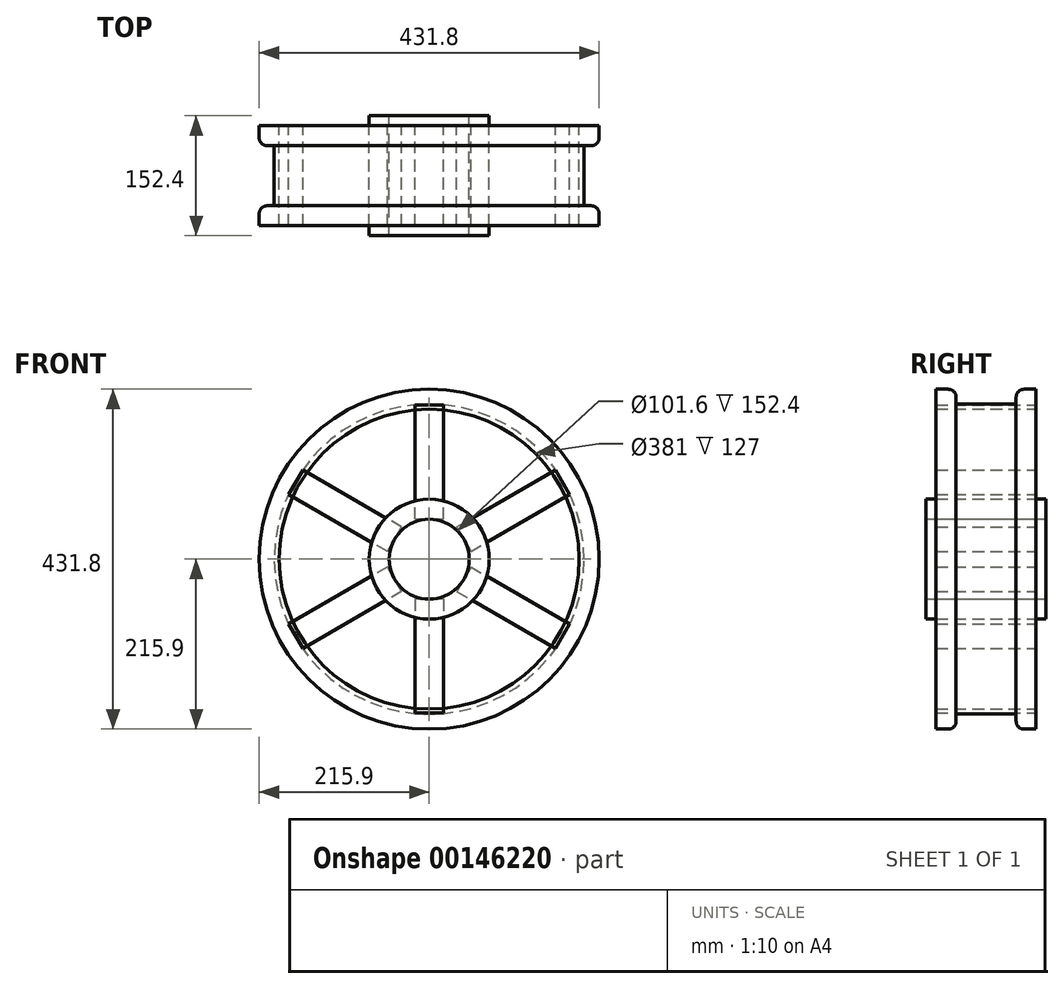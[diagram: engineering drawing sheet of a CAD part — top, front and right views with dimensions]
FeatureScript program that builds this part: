
annotation { "Feature Type Name" : "Feature", "Feature Type Description" : "" }
export const myFeature = defineFeature(function(context is Context, id is Id, definition is map)
    precondition{}
    {
        {
            var Q0;
            Q0=qCreatedBy(makeId("Front.planeOp"),FACE);
            var sketch = newSketch(context, id + "F0", { "sketchPlane" : qUnion([Q0])});
            skCircle(sketch, "E0", {"center": v(0, 0) * mm, "radius": 215.9 * mm});
            skCircle(sketch, "E1", {"center": v(0, 0) * mm, "radius": 190.5 * mm});
            skSolve(sketch);
        }
        {
            var Q0;
            Q0=makeQuery(id+"F0.imprint","IMPRINT",FACE,{"disambiguationData":[TD([[makeQuery(id+"F0.imprint","IMPRINT",EDGE,{"derivedFrom":sQuery(id+"F0.wireOp",EDGE,"E0")}),1.0]])]});
            extrude(context, id + "F1", {"entities" : qUnion([Q0]), "depth" : 127 * mm});
        }
        {
            var Q0;
            Q0=qCreatedBy(makeId("Front.planeOp"),FACE);
            var sketch = newSketch(context, id + "F2", { "sketchPlane" : qUnion([Q0])});
            skCircle(sketch, "E2", {"center": v(0, 0) * mm, "radius": 50.8 * mm});
            skCircle(sketch, "E3", {"center": v(0, 0) * mm, "radius": 76.2 * mm});
            skSolve(sketch);
        }
        {
            var Q0;
            Q0=makeQuery(id+"F2.imprint","IMPRINT",FACE,{"disambiguationData":[TD([[makeQuery(id+"F2.imprint","IMPRINT",EDGE,{"derivedFrom":sQuery(id+"F2.wireOp",EDGE,"E2")}),-1.0]])]});
            extrude(context, id + "F3", {"entities" : qUnion([Q0]), "depth" : 139.7 * mm});
        }
        {
            var Q0;
            Q0=makeQuery(id+"F3.opExtrude","CAP_FACE",FACE,{"disambiguationData":[OSD([sQuery(id+"F2.wireOp",EDGE,"E2"),sQuery(id+"F2.wireOp",EDGE,"E3")])],"isStart":true});
            extrude(context, id + "F4", {"entities" : qUnion([Q0]), "operationType" : NewBodyOperationType.ADD, "depth" : 12.7 * mm});
        }
        {
            var Q0;
            Q0=qCreatedBy(makeId("Front.planeOp"),FACE);
            var sketch = newSketch(context, id + "F5", { "sketchPlane" : qUnion([Q0])});
            skLineSegment(sketch, "E4", {"start": v(-17.98, 50.8) * mm, "end": v(17.98, 50.8) * mm});
            skLineSegment(sketch, "E5", {"start": v(17.98, 50.8) * mm, "end": v(17.98, 195.58) * mm});
            skLineSegment(sketch, "E6", {"start": v(17.98, 195.58) * mm, "end": v(-17.98, 195.58) * mm});
            skLineSegment(sketch, "E7", {"start": v(-17.98, 50.8) * mm, "end": v(-17.98, 195.58) * mm});
            skLineSegment(sketch, "E8.1.0", {"start": v(-160.39, 113.36) * mm, "end": v(-178.37, 82.22) * mm});
            skLineSegment(sketch, "E8.1.1", {"start": v(-35, 40.97) * mm, "end": v(-160.39, 113.36) * mm});
            skLineSegment(sketch, "E8.1.2", {"start": v(-52.99, 9.83) * mm, "end": v(-178.37, 82.22) * mm});
            skLineSegment(sketch, "E8.1.3", {"start": v(-52.99, 9.83) * mm, "end": v(-35, 40.97) * mm});
            skLineSegment(sketch, "E8.2.0", {"start": v(-178.37, -82.22) * mm, "end": v(-160.39, -113.36) * mm});
            skLineSegment(sketch, "E8.2.1", {"start": v(-52.99, -9.83) * mm, "end": v(-178.37, -82.22) * mm});
            skLineSegment(sketch, "E8.2.2", {"start": v(-35, -40.97) * mm, "end": v(-160.39, -113.36) * mm});
            skLineSegment(sketch, "E8.2.3", {"start": v(-35, -40.97) * mm, "end": v(-52.99, -9.83) * mm});
            skLineSegment(sketch, "E8.3.0", {"start": v(-17.98, -195.58) * mm, "end": v(17.98, -195.58) * mm});
            skLineSegment(sketch, "E8.3.1", {"start": v(-17.98, -50.8) * mm, "end": v(-17.98, -195.58) * mm});
            skLineSegment(sketch, "E8.3.2", {"start": v(17.98, -50.8) * mm, "end": v(17.98, -195.58) * mm});
            skLineSegment(sketch, "E8.3.3", {"start": v(17.98, -50.8) * mm, "end": v(-17.98, -50.8) * mm});
            skLineSegment(sketch, "E8.4.0", {"start": v(160.39, -113.36) * mm, "end": v(178.37, -82.22) * mm});
            skLineSegment(sketch, "E8.4.1", {"start": v(35, -40.97) * mm, "end": v(160.39, -113.36) * mm});
            skLineSegment(sketch, "E8.4.2", {"start": v(52.99, -9.83) * mm, "end": v(178.37, -82.22) * mm});
            skLineSegment(sketch, "E8.4.3", {"start": v(52.99, -9.83) * mm, "end": v(35, -40.97) * mm});
            skLineSegment(sketch, "E8.5.0", {"start": v(178.37, 82.22) * mm, "end": v(160.39, 113.36) * mm});
            skLineSegment(sketch, "E8.5.1", {"start": v(52.99, 9.83) * mm, "end": v(178.37, 82.22) * mm});
            skLineSegment(sketch, "E8.5.2", {"start": v(35, 40.97) * mm, "end": v(160.39, 113.36) * mm});
            skLineSegment(sketch, "E8.5.3", {"start": v(35, 40.97) * mm, "end": v(52.99, 9.83) * mm});
            skPoint(sketch, "E8.center", {"position": v(0, 0) * mm});
            skSolve(sketch);
        }
        {
            var Q0;
            Q0=makeQuery(id+"F5.imprint","IMPRINT",FACE,{"disambiguationData":[TD([[makeQuery(id+"F5.imprint","IMPRINT",EDGE,{"derivedFrom":sQuery(id+"F5.wireOp",EDGE,"E4")}),1.0]])]});
            var Q1;
            Q1=makeQuery(id+"F5.imprint","IMPRINT",FACE,{"disambiguationData":[TD([[makeQuery(id+"F5.imprint","IMPRINT",EDGE,{"derivedFrom":sQuery(id+"F5.wireOp",EDGE,"E8.1.0")}),1.0]])]});
            var Q2;
            Q2=makeQuery(id+"F5.imprint","IMPRINT",FACE,{"disambiguationData":[TD([[makeQuery(id+"F5.imprint","IMPRINT",EDGE,{"derivedFrom":sQuery(id+"F5.wireOp",EDGE,"E8.2.0")}),1.0]])]});
            var Q3;
            Q3=makeQuery(id+"F5.imprint","IMPRINT",FACE,{"disambiguationData":[TD([[makeQuery(id+"F5.imprint","IMPRINT",EDGE,{"derivedFrom":sQuery(id+"F5.wireOp",EDGE,"E8.3.0")}),1.0]])]});
            var Q4;
            Q4=makeQuery(id+"F5.imprint","IMPRINT",FACE,{"disambiguationData":[TD([[makeQuery(id+"F5.imprint","IMPRINT",EDGE,{"derivedFrom":sQuery(id+"F5.wireOp",EDGE,"E8.4.0")}),1.0]])]});
            var Q5;
            Q5=makeQuery(id+"F5.imprint","IMPRINT",FACE,{"disambiguationData":[TD([[makeQuery(id+"F5.imprint","IMPRINT",EDGE,{"derivedFrom":sQuery(id+"F5.wireOp",EDGE,"E8.5.0")}),1.0]])]});
            extrude(context, id + "F6", {"entities" : qUnion([Q0, Q1, Q2, Q3, Q4, Q5]), "depth" : 127 * mm});
        }
        {
            var Q0;
            Q0=makeQuery(id+"F1.opExtrude","CAP_FACE",FACE,{"disambiguationData":[OSD([sQuery(id+"F0.wireOp",EDGE,"E0"),sQuery(id+"F0.wireOp",EDGE,"E1")])],"isStart":false});
            cPlane(context, id + "F7", {"entities" : qUnion([Q0]), "cplaneType" : CPlaneType.OFFSET, "offset" : 63.5 * mm, "oppositeDirection" : true, "width" : 152.4 * mm, "height" : 152.4 * mm});
        }
        {
            var Q0;
            Q0=qCreatedBy(id+"F7.planeOp",FACE);
            var sketch = newSketch(context, id + "F8", { "sketchPlane" : qUnion([Q0])});
            skCircle(sketch, "E9", {"center": v(0, 0) * mm, "radius": 196.85 * mm});
            skCircle(sketch, "E10", {"center": v(0, 0) * mm, "radius": 227.2 * mm});
            skSolve(sketch);
        }
        {
            var Q0;
            Q0=makeQuery(id+"F8.imprint","IMPRINT",FACE,{"disambiguationData":[TD([[makeQuery(id+"F8.imprint","IMPRINT",EDGE,{"derivedFrom":sQuery(id+"F8.wireOp",EDGE,"E9")}),-1.0]])]});
            extrude(context, id + "F9", {"entities" : qUnion([Q0]), "operationType" : NewBodyOperationType.REMOVE, "depth" : 38.1 * mm});
        }
        {
            var Q0;
            Q0=qCreatedBy(id+"F7.planeOp",FACE);
            var sketch = newSketch(context, id + "F10", { "sketchPlane" : qUnion([Q0])});
            skCircle(sketch, "E11", {"center": v(0, 0) * mm, "radius": 196.85 * mm});
            skCircle(sketch, "E12", {"center": v(0, 0) * mm, "radius": 223.66 * mm});
            skSolve(sketch);
        }
        {
            var Q0;
            Q0=makeQuery(id+"F10.imprint","IMPRINT",FACE,{"disambiguationData":[TD([[makeQuery(id+"F10.imprint","IMPRINT",EDGE,{"derivedFrom":sQuery(id+"F10.wireOp",EDGE,"E11")}),-1.0]])]});
            extrude(context, id + "F11", {"entities" : qUnion([Q0]), "operationType" : NewBodyOperationType.REMOVE, "oppositeDirection" : true, "depth" : 38.1 * mm});
        }
        {
            var Q0;
            Q0=makeQuery(id+"F9.boolean.opBoolean","INTERSECT",EDGE,{"derivedFrom":[makeQuery(id+"F1.opExtrude","SWEPT_FACE",FACE,{"disambiguationData":[OSD([sQuery(id+"F0.wireOp",EDGE,"E0")])]}),makeQuery(id+"F9.opExtrude","CAP_FACE",FACE,{"disambiguationData":[OSD([sQuery(id+"F8.wireOp",EDGE,"E9"),sQuery(id+"F8.wireOp",EDGE,"E10")])],"isStart":false})]});
            var Q1;
            {var subQ0=sQuery(id+"F0.wireOp",EDGE,"E0");Q1=makeQuery(id+"F11.boolean.opBoolean","INTERSECT",EDGE,{"derivedFrom":[makeQuery(id+"F9.boolean.opBoolean","SPLIT",FACE,{"disambiguationData":[TD([makeQuery(id+"F1.opExtrude","CAP_FACE",FACE,{"disambiguationData":[OSD([subQ0,sQuery(id+"F0.wireOp",EDGE,"E1")])],"isStart":true})])],"derivedFrom":makeQuery(id+"F1.opExtrude","SWEPT_FACE",FACE,{"disambiguationData":[OSD([subQ0])]})}),makeQuery(id+"F11.opExtrude","CAP_FACE",FACE,{"disambiguationData":[OSD([sQuery(id+"F10.wireOp",EDGE,"E11"),sQuery(id+"F10.wireOp",EDGE,"E12")])],"isStart":false})]});}
            fillet(context, id + "F12", {"entities" : qUnion([Q0, Q1]), "radius" : 10.16 * mm, "tangentPropagation" : true, "allowEdgeOverflow" : false});
        }
    });
